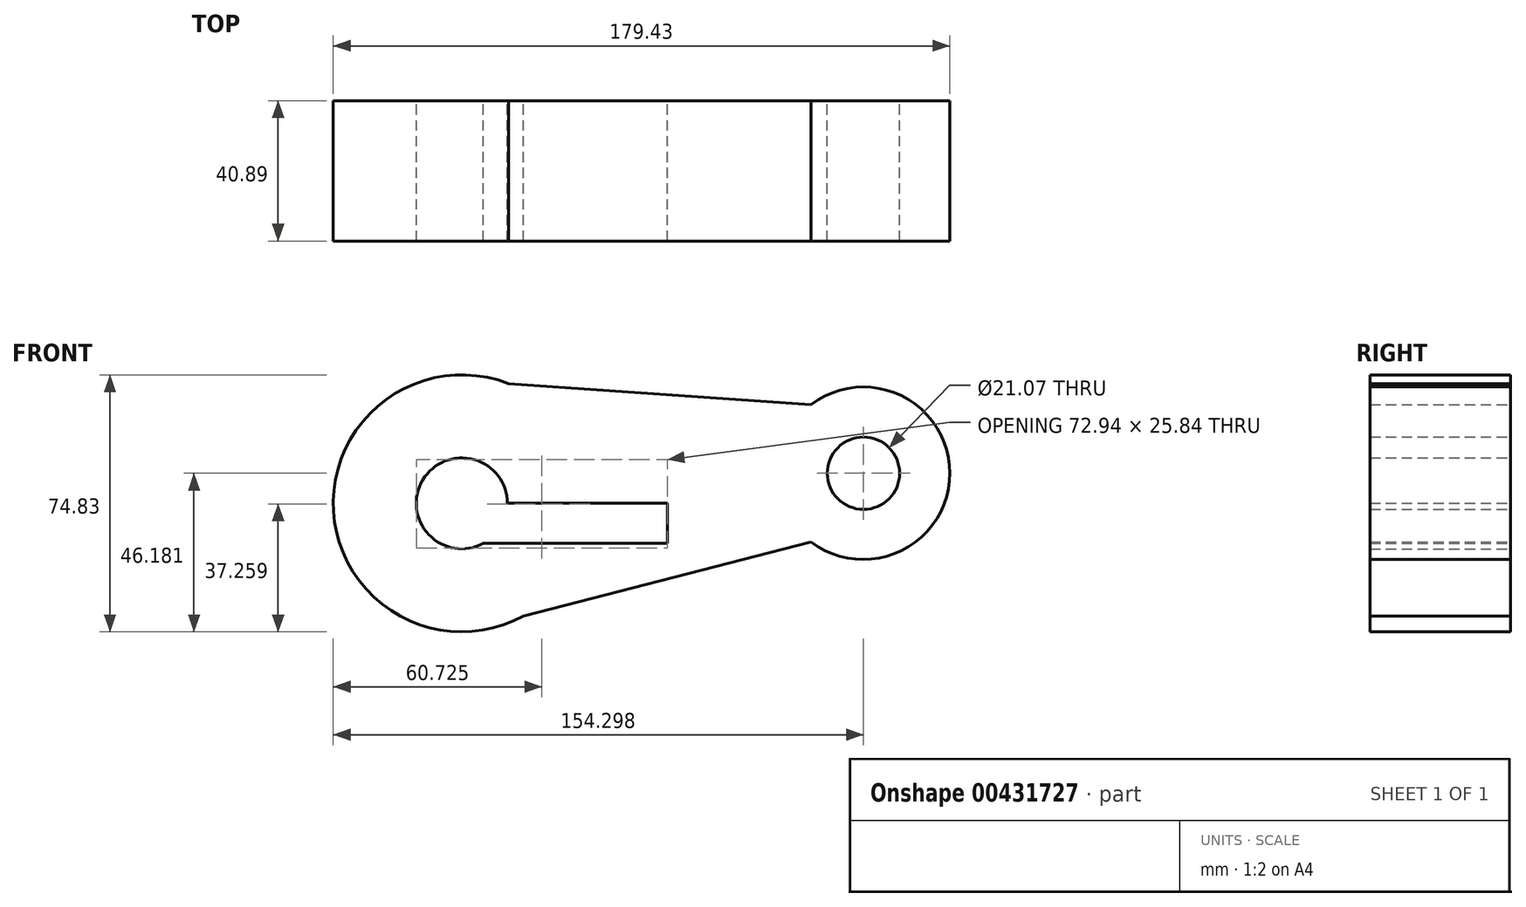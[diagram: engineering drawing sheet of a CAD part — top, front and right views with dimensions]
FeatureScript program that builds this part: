
annotation { "Feature Type Name" : "Feature", "Feature Type Description" : "" }
export const myFeature = defineFeature(function(context is Context, id is Id, definition is map)
    precondition{}
    {
        {
            var Q0;
            Q0=qCreatedBy(makeId("Front.planeOp"),FACE);
            var sketch = newSketch(context, id + "F0", { "sketchPlane" : qUnion([Q0])});
            skCircle(sketch, "E0", {"center": v(-48.7, 27.51) * mm, "radius": 37.42 * mm});
            skCircle(sketch, "E1", {"center": v(68.18, 36.28) * mm, "radius": 25.14 * mm});
            skLineSegment(sketch, "E2", {"start": v(-35.14, 62.4) * mm, "end": v(52.95, 56.28) * mm});
            skLineSegment(sketch, "E3", {"start": v(-30.8, -5.34) * mm, "end": v(52.95, 16.29) * mm});
            skCircle(sketch, "E4", {"center": v(-48.7, 27.51) * mm, "radius": 13.25 * mm});
            skCircle(sketch, "E5", {"center": v(68.18, 36.28) * mm, "radius": 10.54 * mm});
            skPoint(sketch, "E6.oppositeSnap0", {"position": v(11.08, 5.47) * mm});
            skLineSegment(sketch, "E6.bottom", {"start": v(-48.7, 27.51) * mm, "end": v(11.08, 27.51) * mm});
            skLineSegment(sketch, "E6.top", {"start": v(-48.7, 15.83) * mm, "end": v(11.08, 15.83) * mm});
            skLineSegment(sketch, "E6.left", {"start": v(-48.7, 27.51) * mm, "end": v(-48.7, 15.83) * mm});
            skLineSegment(sketch, "E6.right", {"start": v(11.08, 27.51) * mm, "end": v(11.08, 15.83) * mm});
            skSolve(sketch);
        }
        {
            var Q0;
            Q0 = qSketchRegion(id + "F0", true);
            extrude(context, id + "F1", {"entities" : qUnion([Q0]), "depth" : 40.9 * mm});
        }
    });
